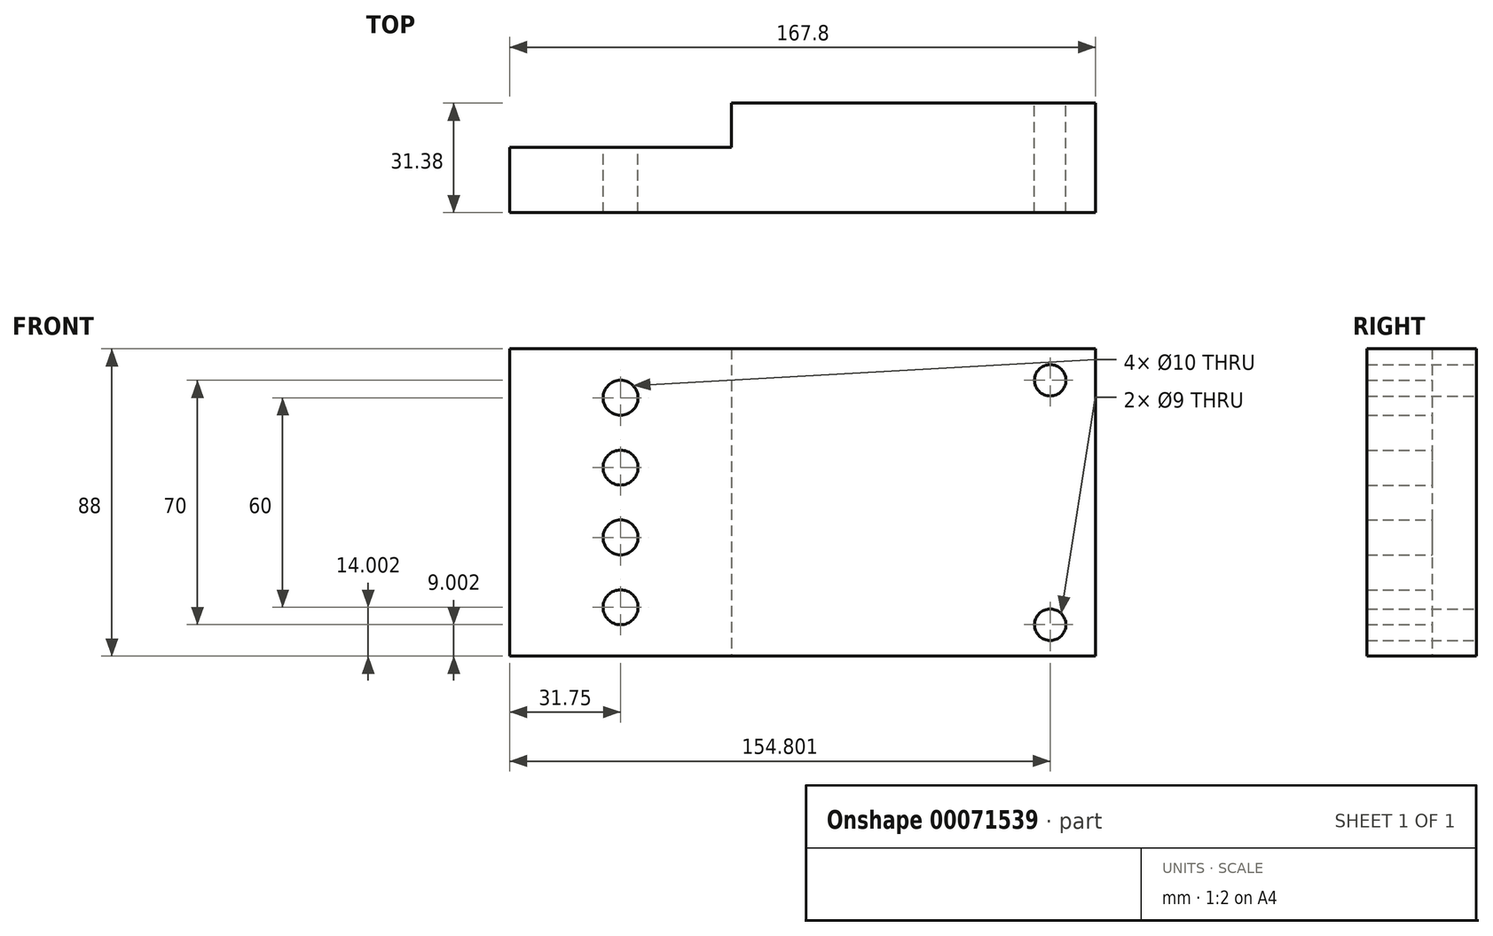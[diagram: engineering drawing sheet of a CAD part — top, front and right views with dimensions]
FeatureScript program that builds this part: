
annotation { "Feature Type Name" : "Feature", "Feature Type Description" : "" }
export const myFeature = defineFeature(function(context is Context, id is Id, definition is map)
    precondition{}
    {
        {
            var Q0;
            Q0=qCreatedBy(makeId("Front.planeOp"),FACE);
            var sketch = newSketch(context, id + "F0", { "sketchPlane" : qUnion([Q0])});
            skLineSegment(sketch, "E0.bottom", {"start": v(-85.18, 32.7) * mm, "end": v(82.62, 32.7) * mm});
            skLineSegment(sketch, "E0.top", {"start": v(-85.18, -55.3) * mm, "end": v(82.62, -55.3) * mm});
            skLineSegment(sketch, "E0.left", {"start": v(-85.18, 32.7) * mm, "end": v(-85.18, -55.3) * mm});
            skLineSegment(sketch, "E0.right", {"start": v(82.62, 32.7) * mm, "end": v(82.62, -55.3) * mm});
            skCircle(sketch, "E1", {"center": v(-53.43, 18.7) * mm, "radius": 5 * mm});
            skCircle(sketch, "E2", {"center": v(69.62, 23.7) * mm, "radius": 4.5 * mm});
            skCircle(sketch, "E3.0.1.0", {"center": v(69.62, -46.3) * mm, "radius": 4.5 * mm});
            skLineSegment(sketch, "E3.direction1", {"start": v(69.62, 23.7) * mm, "end": v(100.24, 23.7) * mm, "construction": true});
            skLineSegment(sketch, "E3.direction2", {"start": v(69.62, 23.7) * mm, "end": v(69.62, -46.3) * mm, "construction": true});
            skCircle(sketch, "E4.0.1.0", {"center": v(-53.43, -1.3) * mm, "radius": 5 * mm});
            skCircle(sketch, "E4.0.2.0", {"center": v(-53.43, -21.3) * mm, "radius": 5 * mm});
            skCircle(sketch, "E4.0.3.0", {"center": v(-53.43, -41.3) * mm, "radius": 5 * mm});
            skLineSegment(sketch, "E4.direction1", {"start": v(-53.43, 18.7) * mm, "end": v(-39.8, 18.7) * mm, "construction": true});
            skLineSegment(sketch, "E4.direction2", {"start": v(-53.43, 18.7) * mm, "end": v(-53.43, -1.3) * mm, "construction": true});
            skSolve(sketch);
        }
        {
            var Q0;
            Q0 = qSketchRegion(id + "F0", true);
            extrude(context, id + "F1", {"entities" : qUnion([Q0]), "depth" : 31.38 * mm});
        }
        {
            var Q0;
            Q0=makeQuery(id+"F1.opExtrude","SWEPT_FACE",FACE,{"disambiguationData":[OSD([sQuery(id+"F0.wireOp",EDGE,"E0.top")])]});
            var sketch = newSketch(context, id + "F2", { "sketchPlane" : qUnion([Q0])});
            skLineSegment(sketch, "E5.bottom", {"start": v(-85.18, 0) * mm, "end": v(-21.68, 0) * mm});
            skLineSegment(sketch, "E5.top", {"start": v(-85.18, 12.7) * mm, "end": v(-21.68, 12.7) * mm});
            skLineSegment(sketch, "E5.left", {"start": v(-85.18, 0) * mm, "end": v(-85.18, 12.7) * mm});
            skLineSegment(sketch, "E5.right", {"start": v(-21.68, 0) * mm, "end": v(-21.68, 12.7) * mm});
            skSolve(sketch);
        }
        {
            var Q0;
            Q0 = qSketchRegion(id + "F2", true);
            extrude(context, id + "F3", {"entities" : qUnion([Q0]), "operationType" : NewBodyOperationType.REMOVE, "endBound" : BoundingType.THROUGH_ALL, "oppositeDirection" : true, "depth" : 25 * mm});
        }
    });
